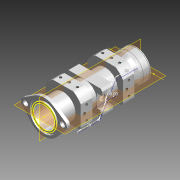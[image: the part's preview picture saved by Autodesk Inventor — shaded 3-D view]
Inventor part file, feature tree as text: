
AUTODESK INVENTOR PART (.ipt)
format: ipt  version: 2015 (Build 190159000, 159)  size: 451,584 bytes
history: native  units: mm
features: sketch x15, projected_geometry x6, extrude x5, hole x5, reference x4, revolve x3, fillet x1, mirror x1
ambient origin geometry x8: Origin, YZ Plane, XZ Plane, XY Plane, X Axis, Y Axis, Z Axis, Center Point
bodies: Solid1 (feature_tree)
feature tree (40):
  revolve  "Revolution1"  [1 undecoded]
  sketch  "Sketch5"  dims[d3=14.0mm d4=120.0mm]
  extrude  "Extrusion2"  Depth=120.0mm
  extrude  "Extrusion3"  Depth=2.0mm
  fillet  "Fillet1"  Radius=1.0mm
  revolve  "Revolution2"  [1 undecoded]
  extrude  "Extrusion4"  TaperAngle=90.0deg  [1 undecoded]
  revolve  "Revolution3"  [1 undecoded]
  extrude  "Extrusion5"  Depth=4.0mm TaperAngle=0.0deg
  extrude  "Extrusion6"  Depth=2.0mm
  hole  "Hole4"  [1 undecoded]
  hole  "Hole5"  [1 undecoded]
  hole  "Hole6"  [1 undecoded]
  sketch  "Sketch17"  dims[d58=20.0mm d59=20.0mm]
  mirror  "Mirror1"
  hole  "Hole7"  [1 undecoded]
  hole  "Hole8"  [1 undecoded]
  sketch  "Sketch1"  dims[d1=13.5mm d2=21.5mm]
  sketch  "Sketch7"  dims[d5=2.0mm d6=0.4mm d7=1.0mm]
  sketch  "Sketch8"  dims[d8=0.4mm d9=1.0mm]
  sketch  "Sketch9"  dims[d10=8.5mm d11=90.0deg]
  sketch  "Sketch10"  dims[d24=6.5mm d27=6.5mm]
  sketch  "Sketch11"  dims[d28=37.0mm d35=4.0mm d36=0.0mm]
  projected_geometry  "Projected Loop2"
  sketch  "Sketch12"  dims[d37=2.0mm d38=0.0mm d39=2.0mm]
  sketch  "Sketch13"  dims[d42=14.0mm d47=10.5mm]
  sketch  "Sketch14"  dims[d49=90.0deg d50=8.0mm]
  projected_geometry  "Projected Loop3"
  sketch  "Sketch15"  dims[d53=8.0mm d54=0.0mm]
  reference  "Reference1"
  reference  "Reference2"
  sketch  "Sketch16"  dims[d55=10.5mm d57=35.0mm]
  reference  "Reference3"
  reference  "Reference4"
  sketch  "Sketch18"  dims[d60=35.0mm]
  projected_geometry  "Projected Loop4"
  projected_geometry  "Projected Loop5"
  sketch  "Sketch19"  dims[d61=10.5mm d62=11.0mm d63=90.0deg d64=7.0mm d65=0.0mm d66=0.0mm d67=0.0mm d68=0.0mm d69=7.0mm d86=4.0mm d87=4.0mm d88=9.0mm d89=9.0mm d90=3.242mm d91=5.0mm d92=4.0mm d93=2.0mm d94=90.0deg d95=6.0mm d96=20.594885mm d97=4.134mm d98=5.0mm d99=4.0mm d100=2.0mm d101=90.0deg d102=7.0mm d103=20.594885mm d104=4.134mm d105=5.0mm d106=4.0mm d107=2.0mm d108=90.0deg d109=7.0mm d110=20.594885mm d113=7.0mm d118=20.0mm d119=60.0deg d120=29.0mm d121=20.0mm d123=29.0mm d124=19.0mm d125=2.0mm d126=2.0mm d127=2.0mm d129=4.0mm d130=6.0mm d131=4.0mm d132=2.0mm d133=90.0deg d134=8.0mm d135=20.594885mm d137=3.242mm d138=8.0mm d139=4.0mm d140=2.0mm d141=90.0deg d142=6.0mm d143=20.594885mm d144=22.0mm d145=22.0mm d146=0.0mm d147=60.0mm d148=3.5mm d149=22.0mm d150=6.0mm d151=6.0mm d152=3.5mm d155=48.0mm d157=24.0mm]
  projected_geometry  "Projected Loop6"
  projected_geometry  "Projected Loop7"
note: 9 required parameter values undecoded (feature->parameter linkage not recoverable at this tier; creation-order binding heuristic only, values carry confidence <= 0.55)